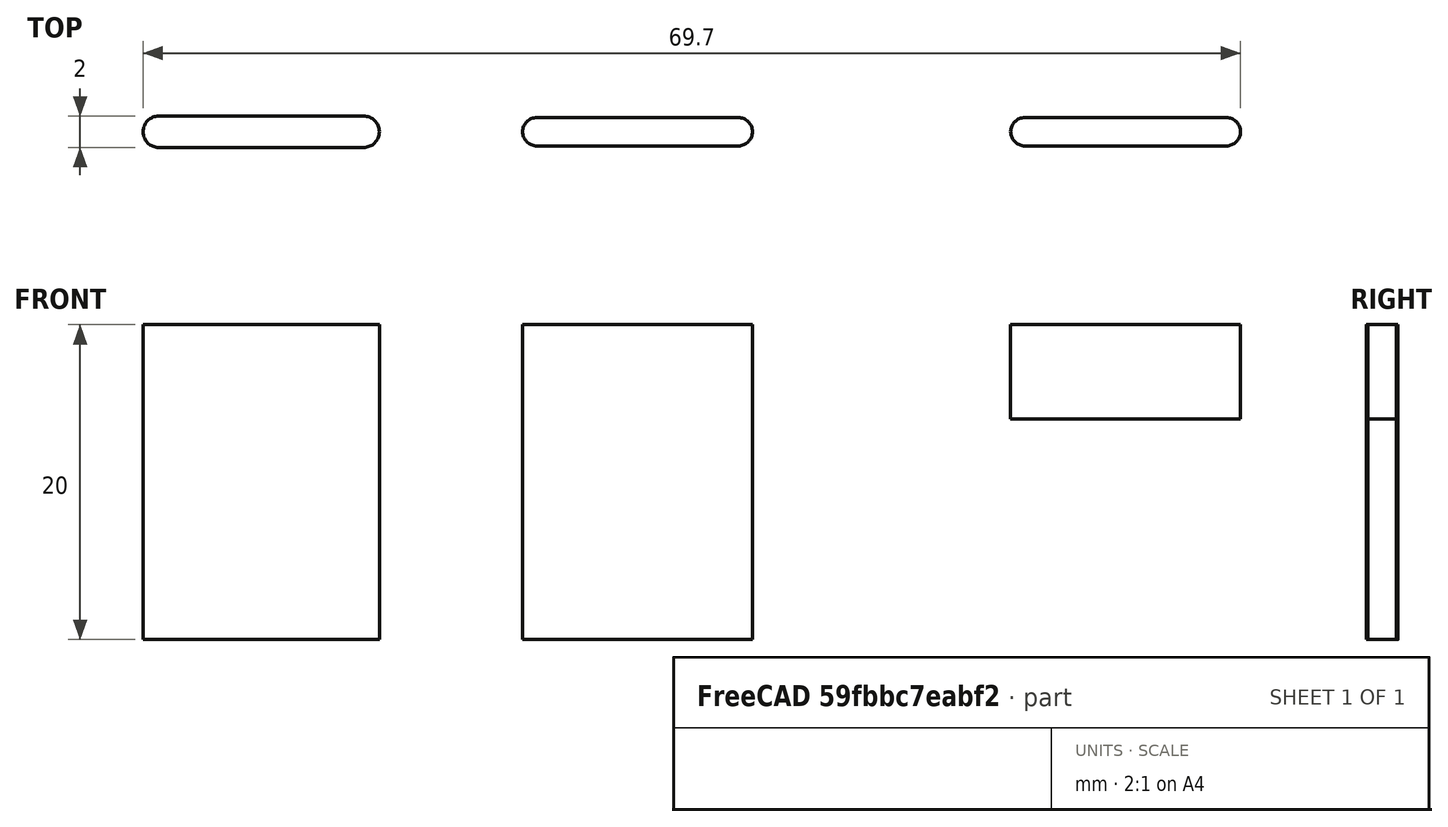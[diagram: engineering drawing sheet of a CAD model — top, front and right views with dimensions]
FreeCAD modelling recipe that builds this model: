
FCSTD DOCUMENT  (FreeCAD 0.17R13522 (Git))
Label: encastradores_cortadores
License: CreativeCommons Attribution-ShareAlike
LicenseURL: http://creativecommons.org/licenses/by-sa/4.0/
objects: Part::Feature×2, Sketcher::SketchObject×1, PartDesign::Pad×1, PartDesign::Body×1, Part::Box×1, Part::Cut×1
note: 8 computed .brp shape members not serialized (recipe doc carries the construction recipe); baked Part::Feature solids carry a one-line shape summary decoded from their .brp

FEATURE [Sketcher::SketchObject] Sketch
  MapMode = 5
  Support = -> [XY_Plane]
  sketch-geometry (4):
    g0: ArcOfCircle CenterX=0 CenterY=0 CenterZ=0 NormalX=0 NormalY=0 NormalZ=1 AngleXU=0 Radius=0.9 StartAngle=1.5708 EndAngle=4.71239
    g1: ArcOfCircle CenterX=12.8 CenterY=0 CenterZ=0 NormalX=0 NormalY=0 NormalZ=1 AngleXU=0 Radius=0.9 StartAngle=4.71239 EndAngle=7.85398
    g2: LineSegment StartX=0 StartY=-0.9 StartZ=0 EndX=12.8 EndY=-0.9 EndZ=0
    g3: LineSegment StartX=0 StartY=0.9 StartZ=0 EndX=12.8 EndY=0.9 EndZ=0
  constraints (9):
    c: Tangent(g0,g3) = 1.5708
    c: Tangent(g0,g2) = -1.5708
    c: Tangent(g2,g1) = -1.5708
    c: Tangent(g3,g1) = 1.5708
    c: Horizontal(g2)
    c: Equal(g0,g1)
    c: Coincident(g0,g-1)
    c: DistanceY(g0,g0) = 1.8
    c: DistanceX(g-1,g1) = 12.8
FEATURE [PartDesign::Pad] Pad
  Length = 20
  Length2 = 100
  Profile = -> Sketch
  Type = 0
FEATURE [PartDesign::Body] Body  label="encastres"
  Group = -> [Sketch,Pad]
  Origin = -> Origin
  Placement = pos=(24,0,0) rot=(0,0,1;0rad)
  Tip = -> Pad
FEATURE [Part::Feature] Body001  label="cortador_parea_encastres"
  shape: bbox 15 x 2 x 20 mm, 6 faces (baked)
FEATURE [Part::Feature] Body002  label="encastres001"
  Placement = pos=(55,0,0) rot=(0,0,1;0rad)
  shape: bbox 14.6 x 1.8 x 20 mm, 6 faces (baked)
FEATURE [Part::Box] Box  label="Cube"
  AttacherType = Attacher::AttachEngine3D
  Height = 14
  Length = 23
  Placement = pos=(52,-4,0) rot=(0,0,1;0rad)
  Width = 10
FEATURE [Part::Cut] Cut
  Base = -> Body002
  Tool = -> Box
